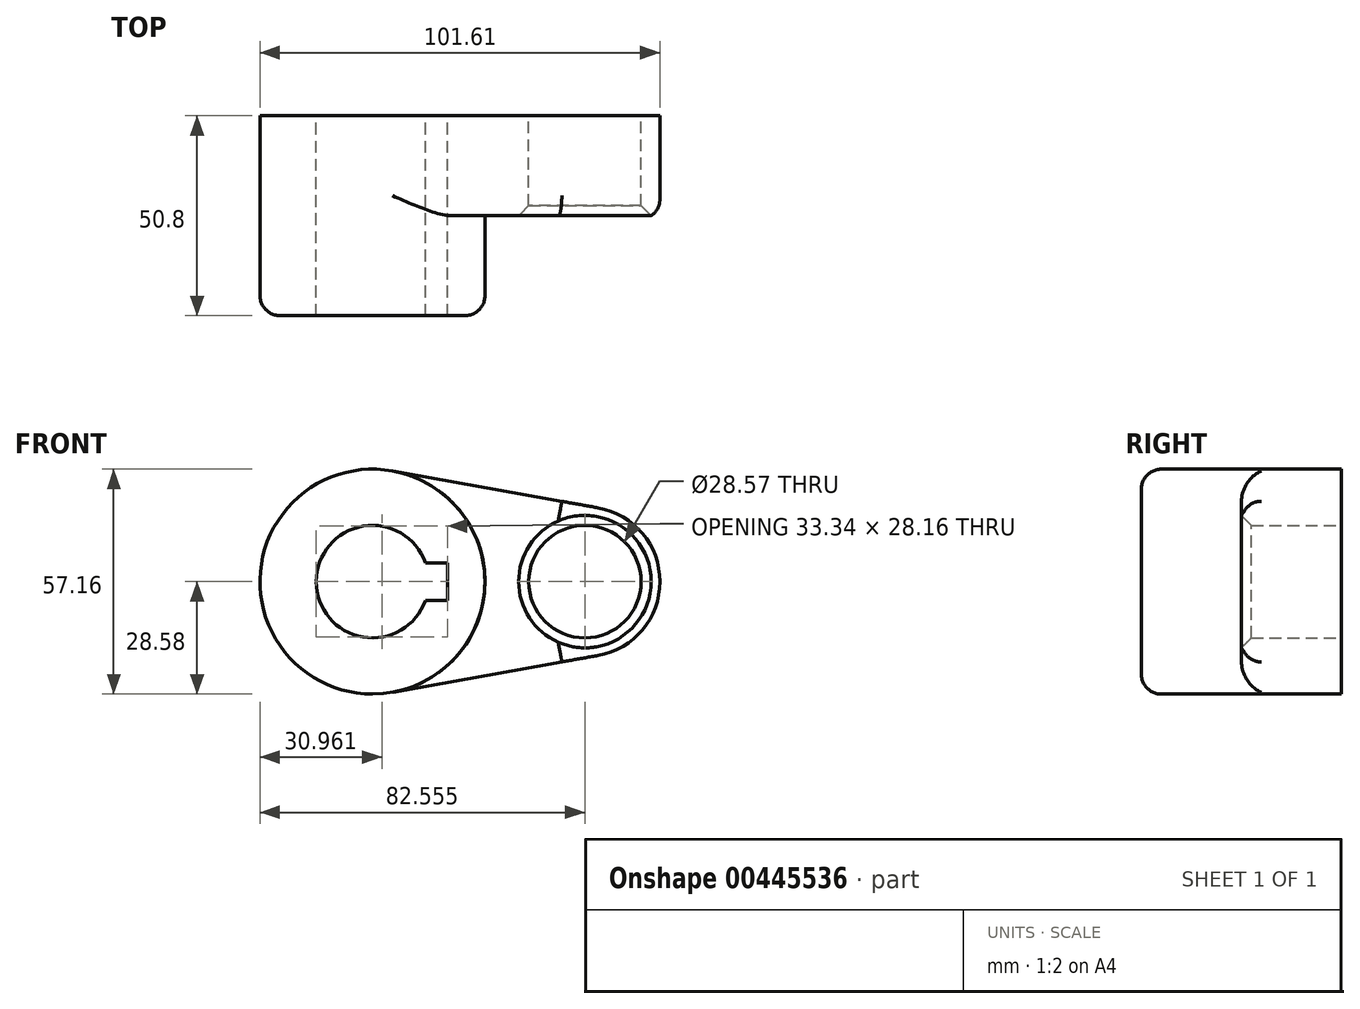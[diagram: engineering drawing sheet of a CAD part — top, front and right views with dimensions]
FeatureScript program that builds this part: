
annotation { "Feature Type Name" : "Feature", "Feature Type Description" : "" }
export const myFeature = defineFeature(function(context is Context, id is Id, definition is map)
    precondition{}
    {
        {
            var Q0;
            Q0=qCreatedBy(makeId("Front.planeOp"),FACE);
            var sketch = newSketch(context, id + "F0", { "sketchPlane" : qUnion([Q0])});
            skCircle(sketch, "E0", {"center": v(0, 0) * mm, "radius": 28.58 * mm});
            skCircle(sketch, "E1", {"center": v(53.97, 0) * mm, "radius": 19.05 * mm});
            skCircle(sketch, "E2", {"center": v(0, 0) * mm, "radius": 14.29 * mm});
            skCircle(sketch, "E3", {"center": v(53.97, 0) * mm, "radius": 14.29 * mm});
            skLineSegment(sketch, "E4.bottom", {"start": v(-19.05, 4.76) * mm, "end": v(19.05, 4.76) * mm});
            skLineSegment(sketch, "E4.top", {"start": v(-19.05, -4.76) * mm, "end": v(19.05, -4.76) * mm});
            skLineSegment(sketch, "E4.left", {"start": v(-19.05, 4.76) * mm, "end": v(-19.05, -4.76) * mm});
            skLineSegment(sketch, "E4.right", {"start": v(19.05, 4.76) * mm, "end": v(19.05, -4.76) * mm});
            skLineSegment(sketch, "E5", {"start": v(5.04, 28.13) * mm, "end": v(57.34, 18.75) * mm});
            skLineSegment(sketch, "E6", {"start": v(5.04, -28.13) * mm, "end": v(57.34, -18.75) * mm});
            skSolve(sketch);
        }
        {
            var Q0;
            {var subQ4=sQuery(id+"F0.wireOp",EDGE,"E4.left");Q0=makeQuery(id+"F0.imprint","IMPRINT",FACE,{"disambiguationData":[TD([[makeQuery(id+"F0.imprint","IMPRINT",EDGE,{"derivedFrom":subQ4}),-1.0]])]});}
            var Q1;
            {var subQ0=sQuery(id+"F0.wireOp",EDGE,"E5");Q1=makeQuery(id+"F0.imprint","IMPRINT",FACE,{"disambiguationData":[TD([[makeQuery(id+"F0.imprint","IMPRINT",EDGE,{"derivedFrom":subQ0}),-1.0]])]});}
            var Q2;
            Q2=makeQuery(id+"F0.imprint","IMPRINT",FACE,{"disambiguationData":[TD([[makeQuery(id+"F0.imprint","IMPRINT",EDGE,{"derivedFrom":sQuery(id+"F0.wireOp",EDGE,"E3")}),-1.0]])]});
            var Q3;
            {var subQ5=sQuery(id+"F0.wireOp",EDGE,"E4.left");Q3=makeQuery(id+"F0.imprint","IMPRINT",FACE,{"disambiguationData":[TD([[makeQuery(id+"F0.imprint","IMPRINT",EDGE,{"derivedFrom":subQ5}),1.0]])]});}
            extrude(context, id + "F1", {"entities" : qUnion([Q0, Q1, Q2, Q3]), "depth" : 25.4 * mm});
        }
        {
            var Q0;
            {var subQ5=sQuery(id+"F0.wireOp",EDGE,"E4.left");Q0=makeQuery(id+"F0.imprint","IMPRINT",FACE,{"disambiguationData":[TD([[makeQuery(id+"F0.imprint","IMPRINT",EDGE,{"derivedFrom":subQ5}),1.0]])]});}
            var Q1;
            {var subQ4=sQuery(id+"F0.wireOp",EDGE,"E4.left");Q1=makeQuery(id+"F0.imprint","IMPRINT",FACE,{"disambiguationData":[TD([[makeQuery(id+"F0.imprint","IMPRINT",EDGE,{"derivedFrom":subQ4}),-1.0]])]});}
            extrude(context, id + "F2", {"entities" : qUnion([Q0, Q1]), "operationType" : NewBodyOperationType.ADD, "depth" : 50.8 * mm});
        }
        {
            var Q0;
            Q0=makeQuery(id+"F2.opExtrude","CAP_EDGE",EDGE,{"disambiguationData":[OSD([sQuery(id+"F0.wireOp",EDGE,"E0")])],"isStart":false});
            fillet(context, id + "F3", {"entities" : qUnion([Q0]), "radius" : 5.08 * mm, "tangentPropagation" : true, "allowEdgeOverflow" : false});
        }
        {
            var Q0;
            Q0=makeQuery(id+"F1.opExtrude","CAP_EDGE",EDGE,{"disambiguationData":[OSD([sQuery(id+"F0.wireOp",EDGE,"E3")])],"isStart":false});
            chamfer(context, id + "F4", {"entities" : qUnion([Q0]), "width" : 2.54 * mm, "tangentPropagation" : true});
        }
        {
            var Q0;
            Q0=makeQuery(id+"F1.opExtrude","CAP_EDGE",EDGE,{"disambiguationData":[OSD([sQuery(id+"F0.wireOp",EDGE,"E6")])],"isStart":false});
            fillet(context, id + "F5", {"entities" : qUnion([Q0]), "radius" : 5.08 * mm, "tangentPropagation" : true, "allowEdgeOverflow" : false});
        }
    });
